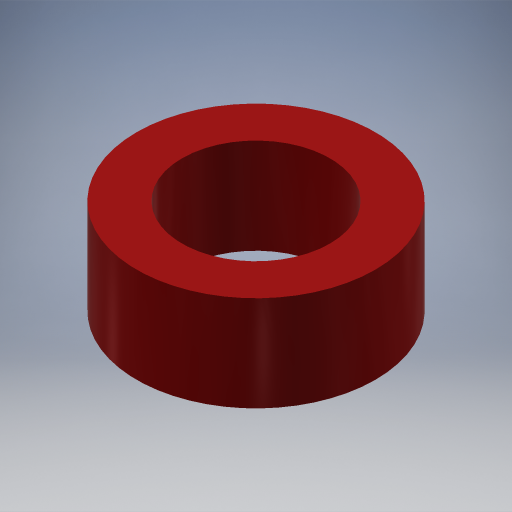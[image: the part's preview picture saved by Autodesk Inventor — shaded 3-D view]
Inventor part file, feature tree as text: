
AUTODESK INVENTOR PART (.ipt)
format: ipt  version: 2024.3 (Build 283343000, 343)  size: 219,136 bytes
history: native  units: mm
features: extrude x1
ambient origin geometry x8: Origin, YZ Plane, XZ Plane, XY Plane, X Axis, Y Axis, Z Axis, Center Point
bodies: Volumenkörper1 (feature_tree)
feature tree (1):
  extrude  "Extrusion1"  Depth=10.0mm
